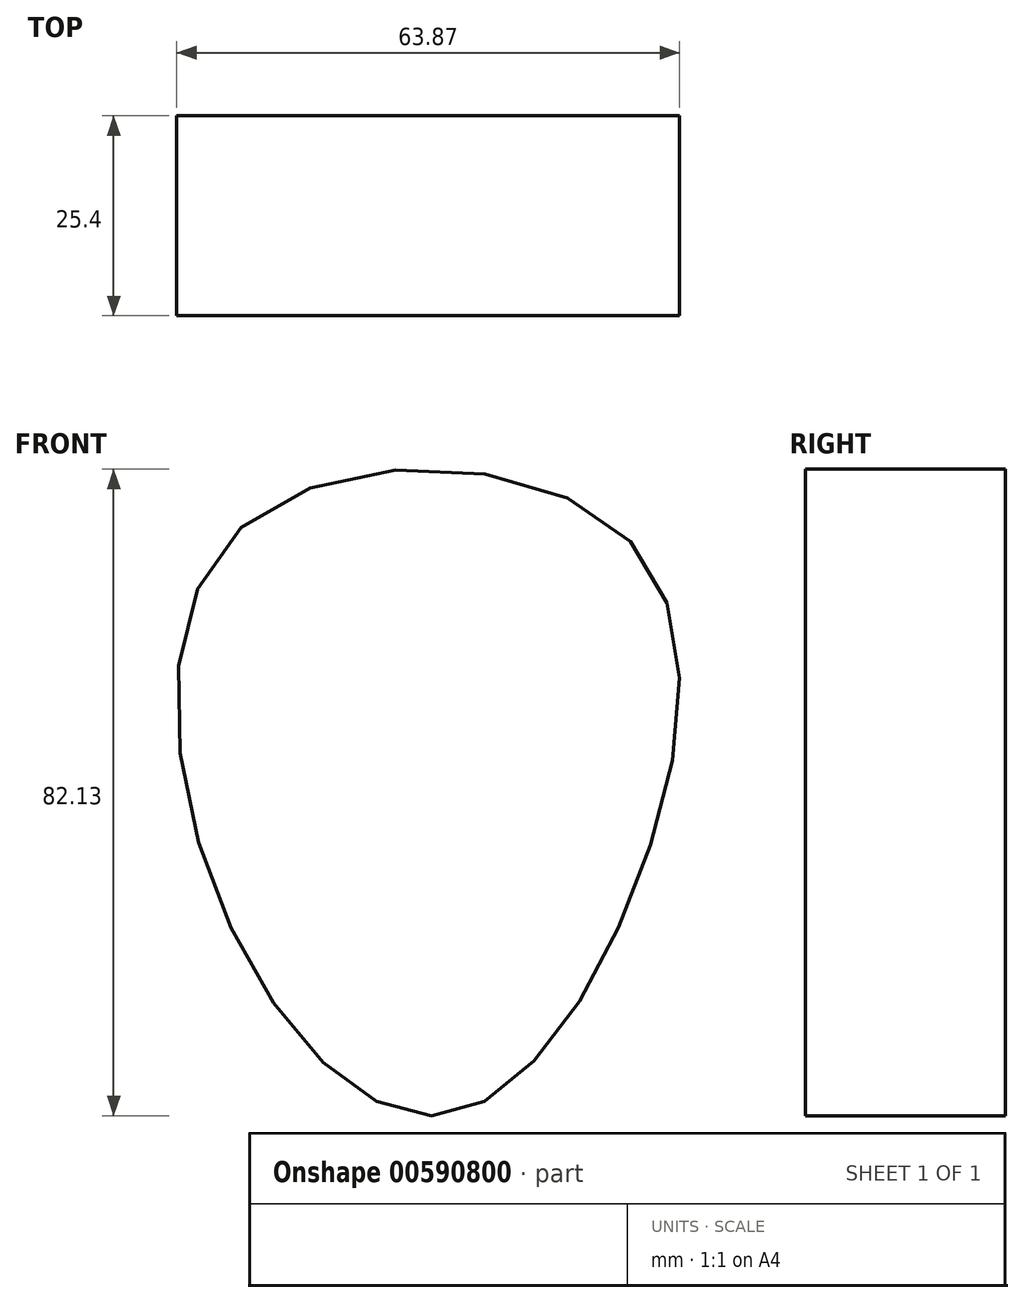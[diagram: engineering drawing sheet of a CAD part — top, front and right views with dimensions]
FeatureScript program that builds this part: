
annotation { "Feature Type Name" : "Feature", "Feature Type Description" : "" }
export const myFeature = defineFeature(function(context is Context, id is Id, definition is map)
    precondition{}
    {
        {
            var Q0;
            Q0=qCreatedBy(makeId("Front.planeOp"),FACE);
            var sketch = newSketch(context, id + "F0", { "sketchPlane" : qUnion([Q0])});
            skFitSpline(sketch, "E0", {"points": [v(-25.2, 33.8) * mm, v(23.38, 32.9) * mm, v(24.58, -12.68) * mm, v(0, -40.87) * mm, v(-26.7, -16.58) * mm, v(-25.2, 33.8) * mm]});
            skSolve(sketch);
        }
        {
            var Q0;
            Q0=makeQuery(id+"F0.imprint","IMPRINT",FACE,{"disambiguationData":[TD([[makeQuery(id+"F0.imprint","IMPRINT",EDGE,{"derivedFrom":sQuery(id+"F0.wireOp",EDGE,"E0")}),-1.0]])]});
            var sketch = newSketch(context, id + "F1", { "sketchPlane" : qUnion([Q0])});
            skCircle(sketch, "E1", {"center": v(-18.17, 15.73) * mm, "radius": 3.73 * mm});
            skCircle(sketch, "E2", {"center": v(14.5, 15.73) * mm, "radius": 3.91 * mm});
            skArc(sketch, "E3", {"start": v(-9.92, 15.73) * mm, "mid": v(-18.17, 20.18) * mm, "end": v(-26.42, 15.73) * mm});
            skArc(sketch, "E4", {"start": v(-26.42, 15.73) * mm, "mid": v(-18.17, 12.02) * mm, "end": v(-9.92, 15.73) * mm});
            skArc(sketch, "E5", {"start": v(21.53, 15.73) * mm, "mid": v(14.05, 19.86) * mm, "end": v(6.57, 15.73) * mm});
            skArc(sketch, "E6", {"start": v(6.57, 15.73) * mm, "mid": v(14.05, 12) * mm, "end": v(21.53, 15.73) * mm});
            skSolve(sketch);
        }
        {
            var Q0;
            Q0=makeQuery(id+"F0.imprint","IMPRINT",FACE,{"disambiguationData":[TD([[makeQuery(id+"F0.imprint","IMPRINT",EDGE,{"derivedFrom":sQuery(id+"F0.wireOp",EDGE,"E0")}),-1.0]])]});
            extrude(context, id + "F2", {"entities" : qUnion([Q0]), "depth" : 25.4 * mm, "offsetDistance" : 25.4 * mm});
        }
    });
